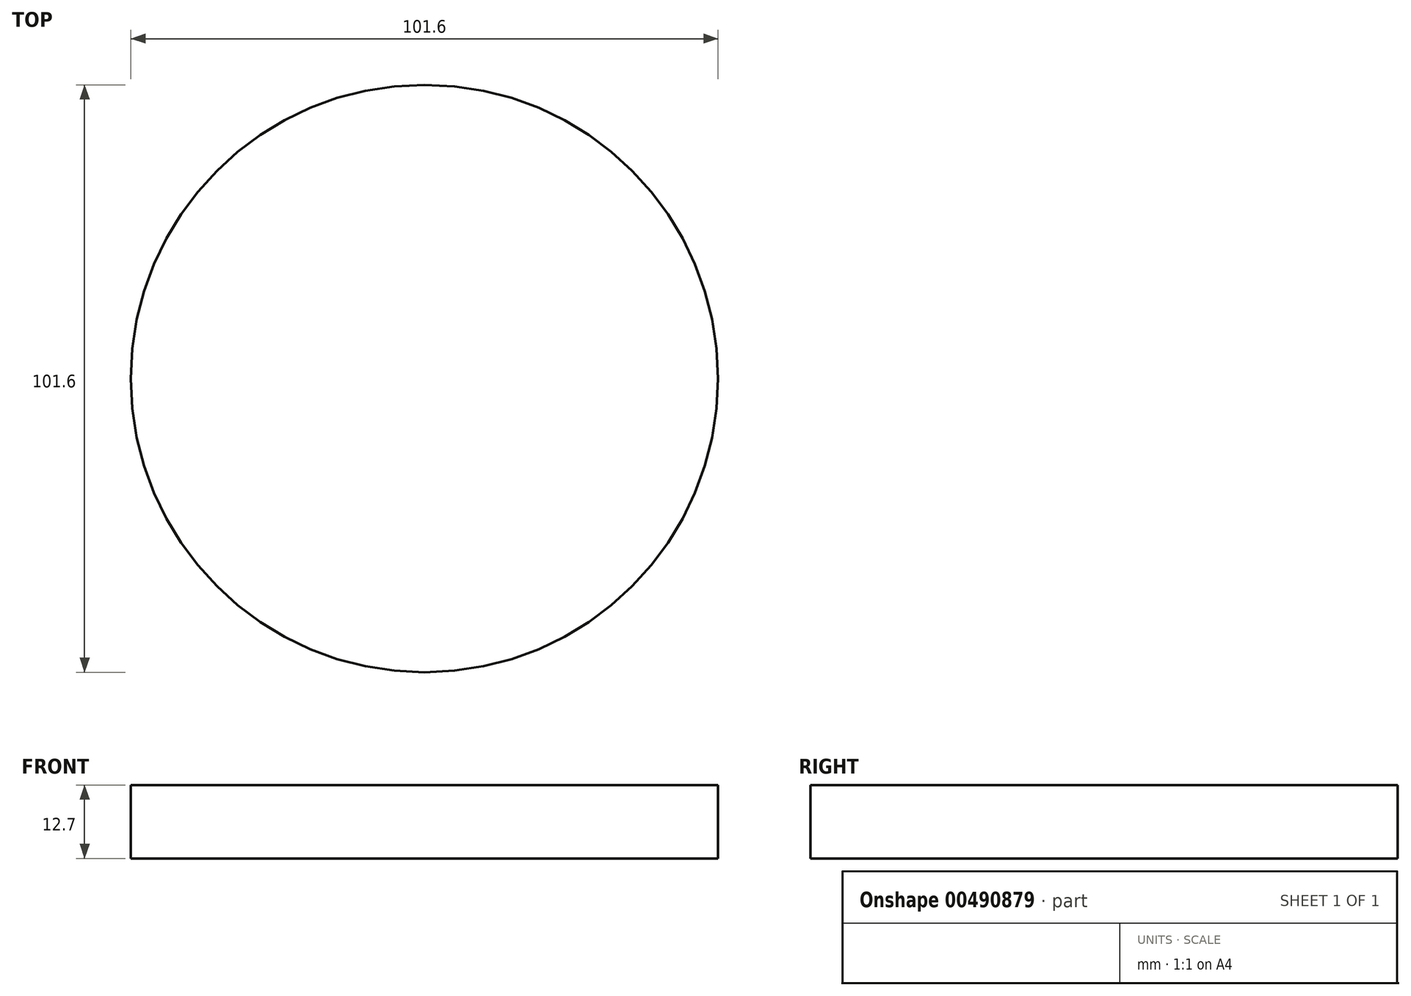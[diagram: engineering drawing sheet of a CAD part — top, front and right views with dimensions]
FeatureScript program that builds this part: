
annotation { "Feature Type Name" : "Feature", "Feature Type Description" : "" }
export const myFeature = defineFeature(function(context is Context, id is Id, definition is map)
    precondition{}
    {
        {
            var Q0;
            Q0=qCreatedBy(makeId("Front.planeOp"),FACE);
            var sketch = newSketch(context, id + "F0", { "sketchPlane" : qUnion([Q0])});
            skLineSegment(sketch, "E0.bottom", {"start": v(25.4, 6.35) * mm, "end": v(-25.4, 6.35) * mm});
            skLineSegment(sketch, "E0.top", {"start": v(25.4, -6.35) * mm, "end": v(-25.4, -6.35) * mm});
            skLineSegment(sketch, "E0.left", {"start": v(25.4, 6.35) * mm, "end": v(25.4, -6.35) * mm});
            skLineSegment(sketch, "E0.right", {"start": v(-25.4, 6.35) * mm, "end": v(-25.4, -6.35) * mm});
            skPoint(sketch, "E0.middle", {"position": v(0, 0) * mm});
            skSolve(sketch);
        }
        {
            var Q0;
            Q0=makeQuery(id+"F0.imprint","IMPRINT",FACE,{"disambiguationData":[TD([[makeQuery(id+"F0.imprint","IMPRINT",EDGE,{"derivedFrom":sQuery(id+"F0.wireOp",EDGE,"E0.bottom")}),1.0]])]});
            var Q1;
            Q1=sQuery(id+"F0.wireOp",EDGE,"E0.left");
            revolve(context, id + "F1", {"entities" : qUnion([Q0]), "axis" : qUnion([Q1]), "revolveType" : RevolveType.FULL});
        }
    });
